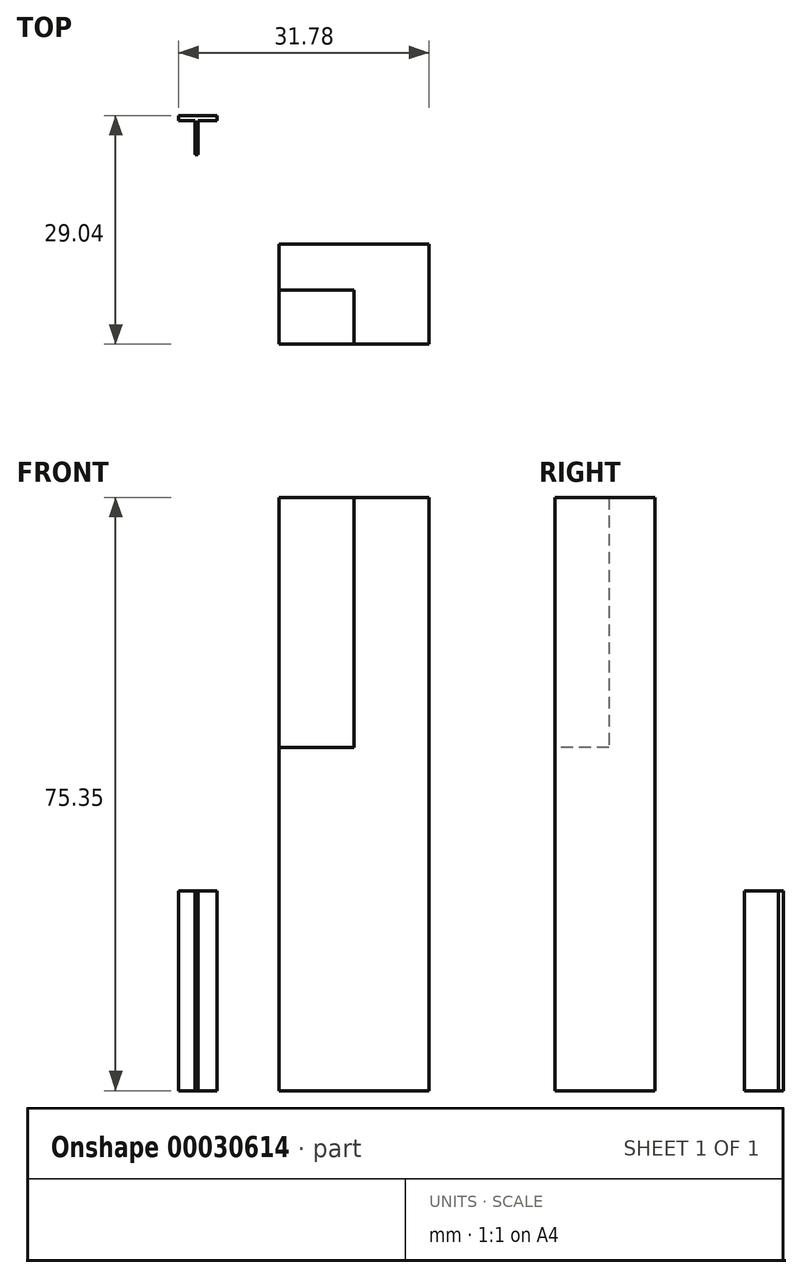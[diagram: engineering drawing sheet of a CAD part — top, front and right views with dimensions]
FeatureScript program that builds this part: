
annotation { "Feature Type Name" : "Feature", "Feature Type Description" : "" }
export const myFeature = defineFeature(function(context is Context, id is Id, definition is map)
    precondition{}
    {
        {
            var Q0;
            Q0=qCreatedBy(makeId("Top.planeOp"),FACE);
            var sketch = newSketch(context, id + "F0", { "sketchPlane" : qUnion([Q0])});
            skLineSegment(sketch, "E0.bottom", {"start": v(-26.94, 28.4) * mm, "end": v(-29.35, 28.4) * mm});
            skLineSegment(sketch, "E0.top", {"start": v(-26.94, 29.04) * mm, "end": v(-31.78, 29.04) * mm});
            skLineSegment(sketch, "E0.left", {"start": v(-26.94, 28.4) * mm, "end": v(-26.94, 29.04) * mm});
            skLineSegment(sketch, "E0.right", {"start": v(-31.78, 28.4) * mm, "end": v(-31.78, 29.04) * mm});
            skLineSegment(sketch, "E1.top", {"start": v(-29.73, 24.05) * mm, "end": v(-29.35, 24.05) * mm});
            skLineSegment(sketch, "E1.left", {"start": v(-29.73, 28.4) * mm, "end": v(-29.73, 24.05) * mm});
            skLineSegment(sketch, "E1.right", {"start": v(-29.35, 28.4) * mm, "end": v(-29.35, 24.05) * mm});
            skLineSegment(sketch, "E2.trimOffspring", {"start": v(-29.73, 28.4) * mm, "end": v(-31.78, 28.4) * mm});
            skSolve(sketch);
        }
        {
            var Q0;
            Q0=makeQuery(id+"F0.imprint","IMPRINT",FACE,{"disambiguationData":[TD([[makeQuery(id+"F0.imprint","IMPRINT",EDGE,{"derivedFrom":sQuery(id+"F0.wireOp",EDGE,"E0.bottom")}),-1.0]])]});
            extrude(context, id + "F1", {"entities" : qUnion([Q0]), "depth" : 25.4 * mm});
        }
        {
            var Q0;
            Q0=qCreatedBy(makeId("Top.planeOp"),FACE);
            var sketch = newSketch(context, id + "F2", { "sketchPlane" : qUnion([Q0])});
            skLineSegment(sketch, "E3.bottom", {"start": v(-19.05, 12.7) * mm, "end": v(0, 12.7) * mm});
            skLineSegment(sketch, "E3.top", {"start": v(-19.05, 0) * mm, "end": v(0, 0) * mm});
            skLineSegment(sketch, "E3.left", {"start": v(-19.05, 12.7) * mm, "end": v(-19.05, 0) * mm});
            skLineSegment(sketch, "E3.right", {"start": v(0, 12.7) * mm, "end": v(0, 0) * mm});
            skSolve(sketch);
        }
        {
            var Q0;
            Q0 = qSketchRegion(id + "F2", true);
            extrude(context, id + "F3", {"entities" : qUnion([Q0]), "depth" : 75.35 * mm});
        }
        {
            var Q0;
            Q0=makeQuery(id+"F3.opExtrude","SWEPT_FACE",FACE,{"disambiguationData":[OSD([sQuery(id+"F2.wireOp",EDGE,"E3.top")])]});
            var sketch = newSketch(context, id + "F4", { "sketchPlane" : qUnion([Q0])});
            skLineSegment(sketch, "E4.bottom", {"start": v(-19.05, 75.35) * mm, "end": v(-9.53, 75.35) * mm});
            skLineSegment(sketch, "E4.top", {"start": v(-19.05, 43.6) * mm, "end": v(-9.52, 43.6) * mm});
            skLineSegment(sketch, "E4.left", {"start": v(-19.05, 75.35) * mm, "end": v(-19.05, 43.6) * mm});
            skLineSegment(sketch, "E4.right", {"start": v(-9.53, 75.35) * mm, "end": v(-9.52, 43.6) * mm});
            skSolve(sketch);
        }
        {
            var Q0;
            Q0 = qSketchRegion(id + "F4", true);
            extrude(context, id + "F5", {"entities" : qUnion([Q0]), "operationType" : NewBodyOperationType.REMOVE, "oppositeDirection" : true, "depth" : 6.87 * mm});
        }
    });
